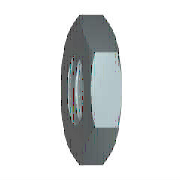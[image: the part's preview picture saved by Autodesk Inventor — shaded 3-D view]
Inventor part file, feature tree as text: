
AUTODESK INVENTOR PART (.ipt)
format: ipt  version: 2020 (Build 240168000, 168)  size: 164,864 bytes
history: native  units: mm (DEFAULTED — no unit token found)
features: sketch x3, extrude x1, chamfer x1, hole x1, other x1, plane x1
ambient origin geometry x7: Origin, YZ Plane, XZ Plane, X Axis, Y Axis, Z Axis, Center Point
bodies: Solid1 (feature_tree)
feature tree (8):
  extrude  "Körper"  Depth=1.2mm
  chamfer  "Fase1"  Angle=30.0deg  [1 undecoded]
  hole  "Gewinde"  [1 undecoded]
  other  "Work Axis1"
  plane  "Work Plane1"
  sketch  "Skizze1"  dims[d0=4.618802mm d1=1.2mm]
  sketch  "Skizze2"  dims[d2=0.0mm]
  sketch  "Skizze3"  dims[d3=30.0deg d4=30.0deg d5=3.1mm d6=3.1mm d7=90.0deg d25=1.567mm d26=6.0mm d27=4.0mm d28=2.0mm d29=14.3117mm d30=8.0mm d31=20.594885mm d8=0.216506mm d9=30.0deg d10=0.216506mm d11=30.0deg d13=0.0mm d14=0.0mm d39=0.0mm d40=0.216506mm d41=0.216506mm d42=0.0mm]
note: 2 required parameter values undecoded (feature->parameter linkage not recoverable at this tier; creation-order binding heuristic only, values carry confidence <= 0.55)
